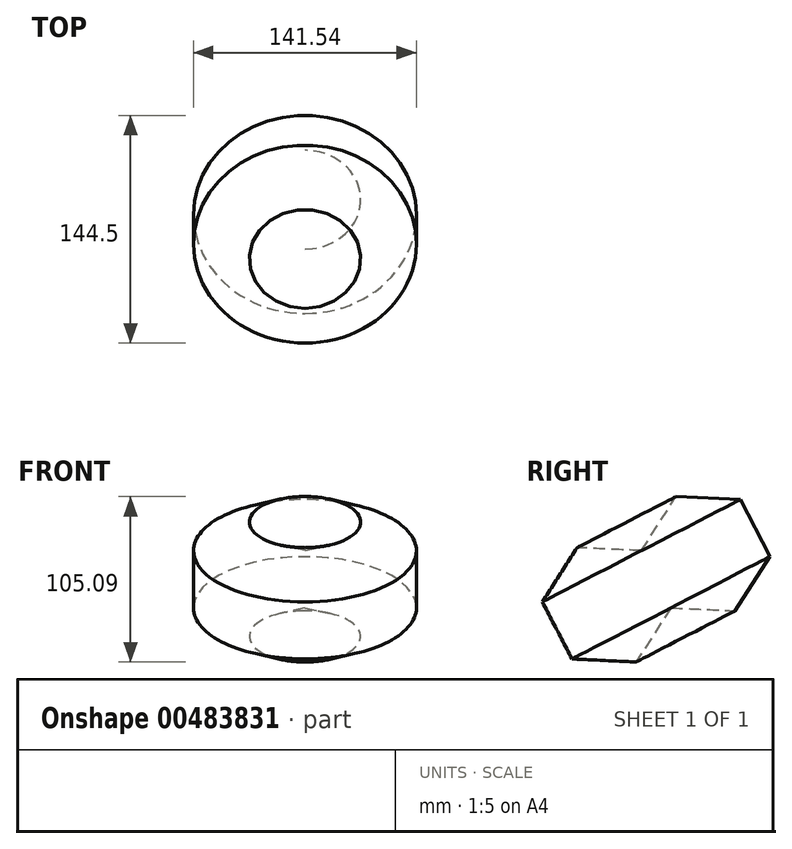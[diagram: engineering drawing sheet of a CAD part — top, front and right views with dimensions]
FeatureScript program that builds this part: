
annotation { "Feature Type Name" : "Feature", "Feature Type Description" : "" }
export const myFeature = defineFeature(function(context is Context, id is Id, definition is map)
    precondition{}
    {
        {
            var Q0;
            Q0=qCreatedBy(makeId("Right.planeOp"),FACE);
            var sketch = newSketch(context, id + "F0", { "sketchPlane" : qUnion([Q0])});
            skCircle(sketch, "E0.cCircle", {"center": v(-38.38, 37.24) * mm, "radius": 35.38 * mm, "construction": true});
            skLineSegment(sketch, "E0.0", {"start": v(2.43, 35.34) * mm, "end": v(-19.62, 0.94) * mm});
            skLineSegment(sketch, "E0.1", {"start": v(-19.62, 0.94) * mm, "end": v(-60.43, 2.84) * mm});
            skLineSegment(sketch, "E0.2", {"start": v(-60.43, 2.84) * mm, "end": v(-79.2, 39.13) * mm});
            skLineSegment(sketch, "E0.3", {"start": v(-79.2, 39.13) * mm, "end": v(-57.15, 73.53) * mm});
            skLineSegment(sketch, "E0.4", {"start": v(-57.15, 73.53) * mm, "end": v(-16.33, 71.63) * mm});
            skLineSegment(sketch, "E0.5", {"start": v(-16.33, 71.63) * mm, "end": v(2.43, 35.34) * mm});
            skPoint(sketch, "E0.0.midPoint", {"position": v(-8.6, 18.14) * mm});
            skSolve(sketch);
        }
        {
            var Q0;
            Q0 = qSketchRegion(id + "F0", true);
            var Q1;
            Q1=sQuery(id+"F0.wireOp",EDGE,"E0.5");
            revolve(context, id + "F1", {"entities" : qUnion([Q0]), "axis" : qUnion([Q1]), "revolveType" : RevolveType.FULL});
        }
    });
